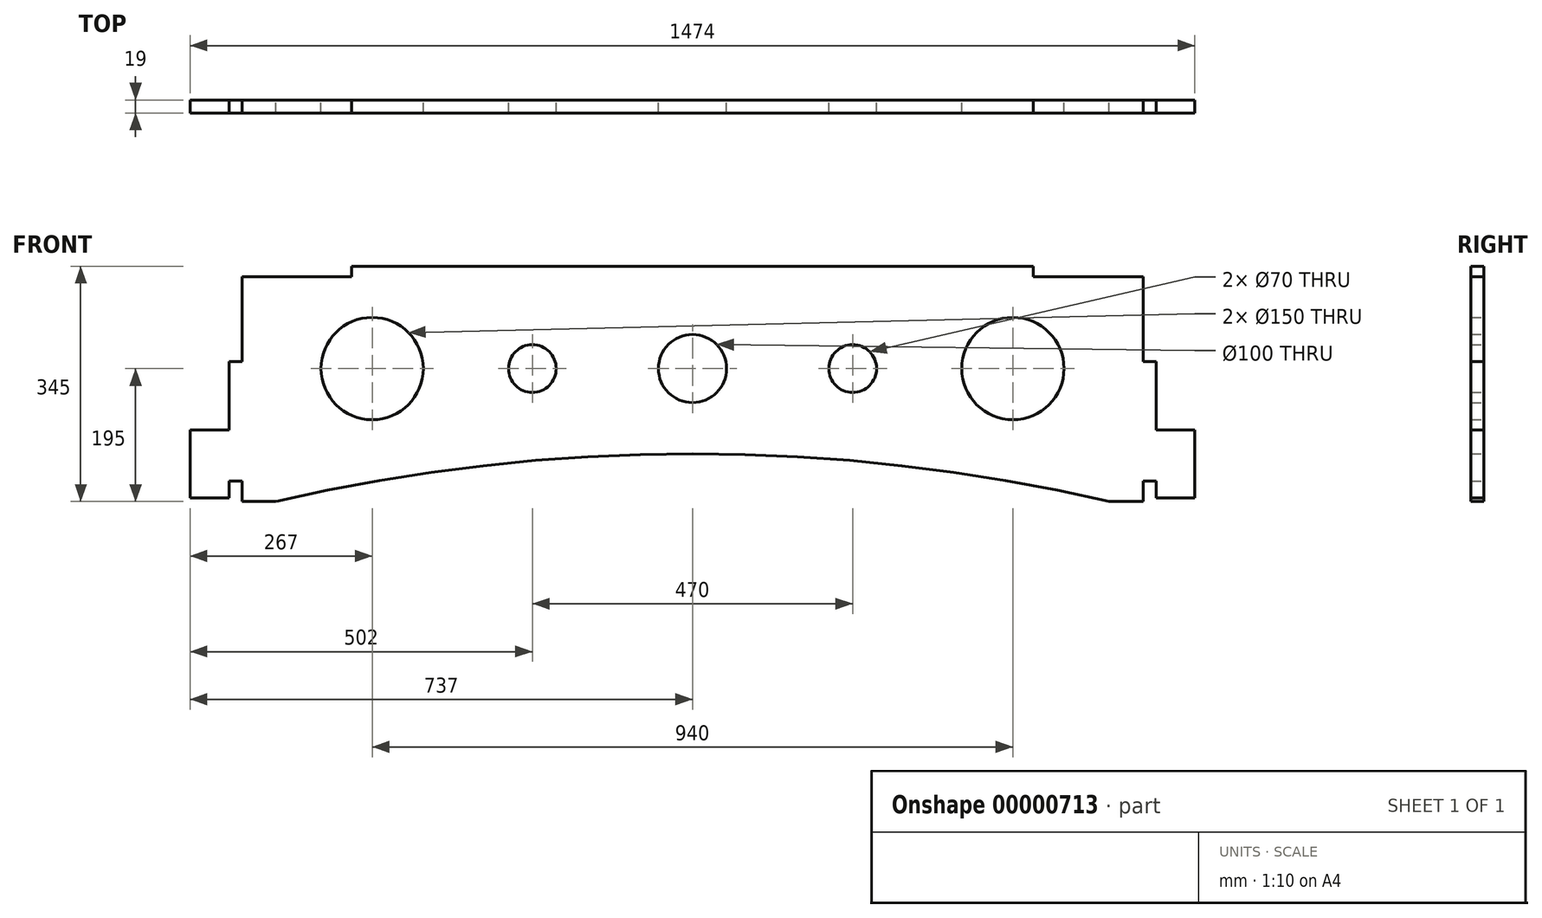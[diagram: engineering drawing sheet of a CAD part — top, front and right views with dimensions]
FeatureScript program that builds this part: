
annotation { "Feature Type Name" : "Feature", "Feature Type Description" : "" }
export const myFeature = defineFeature(function(context is Context, id is Id, definition is map)
    precondition{}
    {
        {
            var Q0;
            Q0=qCreatedBy(makeId("Front.planeOp"),FACE);
            var sketch = newSketch(context, id + "F0", { "sketchPlane" : qUnion([Q0])});
            skLineSegment(sketch, "E0", {"start": v(-500, 0) * mm, "end": v(-500, 15) * mm});
            skLineSegment(sketch, "E1", {"start": v(-500, 15) * mm, "end": v(500, 15) * mm});
            skLineSegment(sketch, "E2", {"start": v(500, 15) * mm, "end": v(500, 0) * mm});
            skLineSegment(sketch, "E3", {"start": v(-500, 0) * mm, "end": v(-661, 0) * mm});
            skLineSegment(sketch, "E4", {"start": v(-661, 0) * mm, "end": v(-661, -125) * mm});
            skLineSegment(sketch, "E5", {"start": v(0, 15) * mm, "end": v(0, 0) * mm, "construction": true});
            skLineSegment(sketch, "E6", {"start": v(500, 0) * mm, "end": v(661, 0) * mm});
            skLineSegment(sketch, "E7", {"start": v(661, 0) * mm, "end": v(661, -125) * mm});
            skLineSegment(sketch, "E8", {"start": v(-661, -125) * mm, "end": v(-680, -125) * mm});
            skLineSegment(sketch, "E9", {"start": v(-680, -125) * mm, "end": v(-680, -225) * mm});
            skLineSegment(sketch, "E10", {"start": v(-680, -225) * mm, "end": v(-737, -225) * mm});
            skLineSegment(sketch, "E11", {"start": v(-737, -225) * mm, "end": v(-737, -325) * mm});
            skLineSegment(sketch, "E12", {"start": v(-737, -325) * mm, "end": v(-680, -325) * mm});
            skLineSegment(sketch, "E13", {"start": v(-680, -325) * mm, "end": v(-680, -300) * mm});
            skLineSegment(sketch, "E14", {"start": v(-680, -300) * mm, "end": v(-661, -300) * mm});
            skLineSegment(sketch, "E15", {"start": v(-661, -300) * mm, "end": v(-661, -330) * mm});
            skLineSegment(sketch, "E16", {"start": v(-661, -330) * mm, "end": v(-611, -330) * mm});
            skLineSegment(sketch, "E17", {"start": v(661, -125) * mm, "end": v(680, -125) * mm});
            skLineSegment(sketch, "E18", {"start": v(680, -125) * mm, "end": v(680, -225) * mm});
            skLineSegment(sketch, "E19", {"start": v(680, -225) * mm, "end": v(737, -225) * mm});
            skLineSegment(sketch, "E20", {"start": v(737, -225) * mm, "end": v(737, -325) * mm});
            skLineSegment(sketch, "E21", {"start": v(737, -325) * mm, "end": v(680, -325) * mm});
            skLineSegment(sketch, "E22", {"start": v(680, -325) * mm, "end": v(680, -300) * mm});
            skLineSegment(sketch, "E23", {"start": v(680, -300) * mm, "end": v(661, -300) * mm});
            skLineSegment(sketch, "E24", {"start": v(661, -300) * mm, "end": v(661, -330) * mm});
            skLineSegment(sketch, "E25", {"start": v(661, -330) * mm, "end": v(611, -330) * mm});
            skArc(sketch, "E26", {"start": v(611, -330) * mm, "mid": v(0, -260) * mm, "end": v(-611, -330) * mm});
            skCircle(sketch, "E27", {"center": v(0, -135) * mm, "radius": 50 * mm});
            skCircle(sketch, "E28", {"center": v(-235, -135) * mm, "radius": 35 * mm});
            skCircle(sketch, "E29", {"center": v(-470, -135) * mm, "radius": 75 * mm});
            skCircle(sketch, "E30", {"center": v(235, -135) * mm, "radius": 35 * mm});
            skCircle(sketch, "E31", {"center": v(470, -135) * mm, "radius": 75 * mm});
            skLineSegment(sketch, "E32", {"start": v(-470, -135) * mm, "end": v(-235, -135) * mm, "construction": true});
            skLineSegment(sketch, "E33", {"start": v(-235, -135) * mm, "end": v(0, -135) * mm, "construction": true});
            skLineSegment(sketch, "E34", {"start": v(0, -135) * mm, "end": v(235, -135) * mm, "construction": true});
            skLineSegment(sketch, "E35", {"start": v(235, -135) * mm, "end": v(470, -135) * mm, "construction": true});
            skSolve(sketch);
        }
        {
            var Q0;
            Q0=makeQuery(id+"F0.imprint","IMPRINT",FACE,{"disambiguationData":[TD([[makeQuery(id+"F0.imprint","IMPRINT",EDGE,{"derivedFrom":sQuery(id+"F0.wireOp",EDGE,"E0")}),-1.0]])]});
            extrude(context, id + "F1", {"entities" : qUnion([Q0]), "depth" : 19 * mm});
        }
    });
